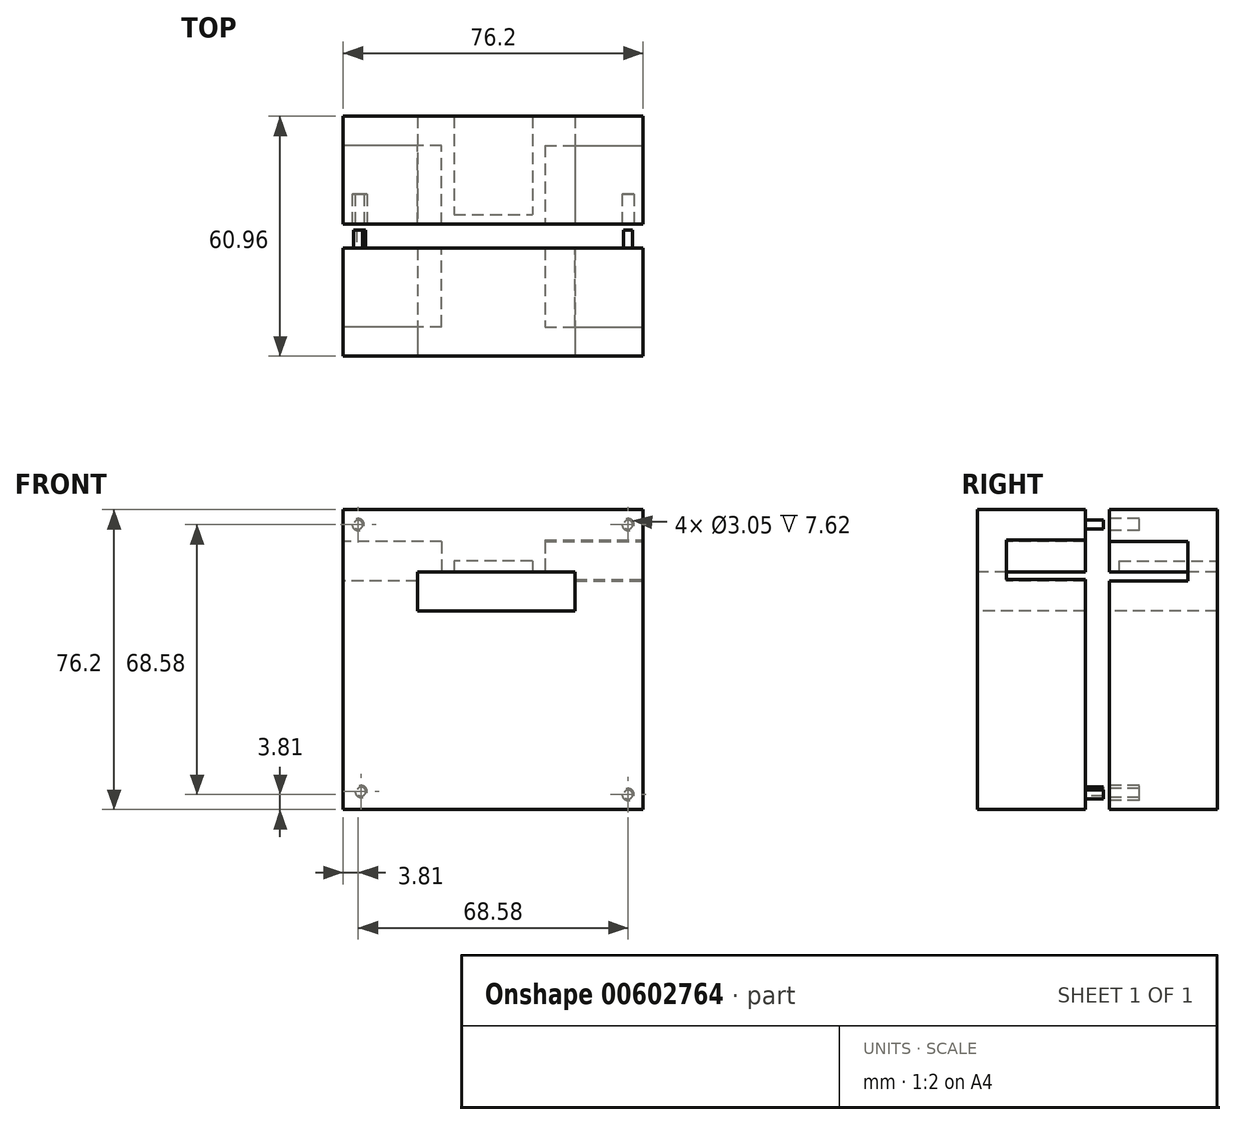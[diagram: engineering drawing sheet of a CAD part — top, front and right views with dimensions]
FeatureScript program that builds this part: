
annotation { "Feature Type Name" : "Feature", "Feature Type Description" : "" }
export const myFeature = defineFeature(function(context is Context, id is Id, definition is map)
    precondition{}
    {
        {
            var Q0;
            Q0=qCreatedBy(makeId("Front.planeOp"),FACE);
            var sketch = newSketch(context, id + "F0", { "sketchPlane" : qUnion([Q0])});
            skLineSegment(sketch, "E0.bottom", {"start": v(-63.5, 63.5) * mm, "end": v(63.5, 63.5) * mm});
            skLineSegment(sketch, "E0.top", {"start": v(-63.5, -63.5) * mm, "end": v(63.5, -63.5) * mm});
            skLineSegment(sketch, "E0.left", {"start": v(-63.5, 63.5) * mm, "end": v(-63.5, -63.5) * mm});
            skLineSegment(sketch, "E0.right", {"start": v(63.5, 63.5) * mm, "end": v(63.5, -63.5) * mm});
            skPoint(sketch, "E0.middle", {"position": v(0, 0) * mm});
            skSolve(sketch);
        }
        {
            var Q0;
            Q0=makeQuery(id+"F0.imprint","IMPRINT",FACE,{"disambiguationData":[TD([[makeQuery(id+"F0.imprint","IMPRINT",EDGE,{"derivedFrom":sQuery(id+"F0.wireOp",EDGE,"E0.bottom")}),-1.0]])]});
            extrude(context, id + "F1", {"entities" : qUnion([Q0]), "endBound" : BoundingType.SYMMETRIC, "depth" : 101.6 * mm, "offsetDistance" : 25.4 * mm});
        }
        {
            var Q0;
            Q0=makeQuery(id+"F1.opExtrude","SWEPT_FACE",FACE,{"disambiguationData":[OSD([sQuery(id+"F0.wireOp",EDGE,"E0.left")])]});
            var sketch = newSketch(context, id + "F2", { "sketchPlane" : qUnion([Q0])});
            skLineSegment(sketch, "E1.bottom", {"start": v(-5.1, 63.5) * mm, "end": v(5.1, 63.5) * mm});
            skLineSegment(sketch, "E1.top", {"start": v(-5.1, -63.5) * mm, "end": v(5.1, -63.5) * mm});
            skLineSegment(sketch, "E1.left", {"start": v(-5.1, 63.5) * mm, "end": v(-5.1, -63.5) * mm});
            skLineSegment(sketch, "E1.right", {"start": v(5.1, 63.5) * mm, "end": v(5.1, -63.5) * mm});
            skPoint(sketch, "E1.middle", {"position": v(0, 0) * mm});
            skPoint(sketch, "E1.middle.positionSnap0", {"position": v(0, 63.5) * mm});
            skPoint(sketch, "E1.middle.positionSnap1", {"position": v(-50.8, 0) * mm});
            skPoint(sketch, "E1.centerSnap0", {"position": v(0, 63.5) * mm});
            skPoint(sketch, "E1.centerSnap1", {"position": v(-50.8, 0) * mm});
            skSolve(sketch);
        }
        {
            var Q0;
            Q0=makeQuery(id+"F2.imprint","IMPRINT",FACE,{"disambiguationData":[TD([[makeQuery(id+"F2.imprint","IMPRINT",EDGE,{"derivedFrom":sQuery(id+"F2.wireOp",EDGE,"E1.bottom")}),1.0]])]});
            extrude(context, id + "F3", {"entities" : qUnion([Q0]), "operationType" : NewBodyOperationType.REMOVE, "oppositeDirection" : true, "depth" : 127 * mm, "offsetDistance" : 25.4 * mm});
        }
        {
            var Q0;
            Q0=makeQuery(id+"F3.boolean.opBoolean","COPY",FACE,{"derivedFrom":makeQuery(id+"F3.opExtrude","SWEPT_FACE",FACE,{"disambiguationData":[OSD([sQuery(id+"F2.wireOp",EDGE,"E1.left")])]})});
            var sketch = newSketch(context, id + "F4", { "sketchPlane" : qUnion([Q0])});
            skCircle(sketch, "E2", {"center": v(-57.15, 57.15) * mm, "radius": 2.54 * mm});
            skCircle(sketch, "E3", {"center": v(57.15, 57.15) * mm, "radius": 2.54 * mm});
            skCircle(sketch, "E4", {"center": v(57.15, -57.15) * mm, "radius": 2.54 * mm});
            skCircle(sketch, "E5", {"center": v(-55.88, -55.88) * mm, "radius": 2.54 * mm});
            skSolve(sketch);
        }
        {
            var Q0;
            Q0=makeQuery(id+"F3.boolean.opBoolean","COPY",FACE,{"derivedFrom":makeQuery(id+"F3.opExtrude","SWEPT_FACE",FACE,{"disambiguationData":[OSD([sQuery(id+"F2.wireOp",EDGE,"E1.right")])]})});
            var sketch = newSketch(context, id + "F5", { "sketchPlane" : qUnion([Q0])});
            skCircle(sketch, "E6", {"center": v(57.15, 57.15) * mm, "radius": 1.9 * mm});
            skCircle(sketch, "E7", {"center": v(-57.15, -57.15) * mm, "radius": 1.9 * mm});
            skCircle(sketch, "E8", {"center": v(-57.15, 57.15) * mm, "radius": 1.9 * mm});
            skCircle(sketch, "E9", {"center": v(55.88, -55.88) * mm, "radius": 1.9 * mm});
            skSolve(sketch);
        }
        {
            var Q0;
            Q0 = qSketchRegion(id + "F4", true);
            extrude(context, id + "F6", {"entities" : qUnion([Q0]), "operationType" : NewBodyOperationType.REMOVE, "oppositeDirection" : true, "depth" : 12.7 * mm, "offsetDistance" : 25.4 * mm});
        }
        {
            var Q0;
            Q0 = qSketchRegion(id + "F5", true);
            extrude(context, id + "F7", {"entities" : qUnion([Q0]), "operationType" : NewBodyOperationType.ADD, "depth" : 7.62 * mm, "offsetDistance" : 25.4 * mm});
        }
        {
            var Q0;
            Q0=makeQuery(id+"F3.boolean.opBoolean","SPLIT",BODY,{"disambiguationData":[OD(1.0)],"derivedFrom":makeQuery(id+"F1.opExtrude","SWEPT_BODY",BODY,{"disambiguationData":[OSD([sQuery(id+"F0.wireOp",EDGE,"E0.bottom"),sQuery(id+"F0.wireOp",EDGE,"E0.top"),sQuery(id+"F0.wireOp",EDGE,"E0.left"),sQuery(id+"F0.wireOp",EDGE,"E0.right")])]})});
            var Q1;
            Q1=makeQuery(id+"F3.boolean.opBoolean","SPLIT",BODY,{"disambiguationData":[OD(0.0)],"derivedFrom":makeQuery(id+"F1.opExtrude","SWEPT_BODY",BODY,{"disambiguationData":[OSD([sQuery(id+"F0.wireOp",EDGE,"E0.bottom"),sQuery(id+"F0.wireOp",EDGE,"E0.top"),sQuery(id+"F0.wireOp",EDGE,"E0.left"),sQuery(id+"F0.wireOp",EDGE,"E0.right")])]})});
            var Q2;
            Q2=qCreatedBy(makeId("Origin.pointOp"),VERTEX);
            transform(context, id + "F8", {"entities" : qUnion([Q0, Q1]), "transformType" : TransformType.SCALE_UNIFORMLY, "scale" : 0.6, "scalePoint" : qUnion([Q2]), "makeCopy" : false});
        }
        {
            var Q0;
            Q0=makeQuery(id+"F1.opExtrude","CAP_FACE",FACE,{"disambiguationData":[OSD([sQuery(id+"F0.wireOp",EDGE,"E0.bottom"),sQuery(id+"F0.wireOp",EDGE,"E0.top"),sQuery(id+"F0.wireOp",EDGE,"E0.left"),sQuery(id+"F0.wireOp",EDGE,"E0.right")])],"isStart":false});
            var sketch = newSketch(context, id + "F9", { "sketchPlane" : qUnion([Q0])});
            skLineSegment(sketch, "E10.bottom", {"start": v(-19.17, 22.33) * mm, "end": v(20.83, 22.33) * mm});
            skLineSegment(sketch, "E10.top", {"start": v(-19.17, 12.33) * mm, "end": v(20.83, 12.33) * mm});
            skLineSegment(sketch, "E10.left", {"start": v(-19.17, 22.33) * mm, "end": v(-19.17, 12.33) * mm});
            skLineSegment(sketch, "E10.right", {"start": v(20.83, 22.33) * mm, "end": v(20.83, 12.33) * mm});
            skPoint(sketch, "E10.middle", {"position": v(0.83, 17.33) * mm});
            skSolve(sketch);
        }
        {
            var Q0;
            Q0 = qSketchRegion(id + "F9", true);
            extrude(context, id + "F10", {"entities" : qUnion([Q0]), "operationType" : NewBodyOperationType.REMOVE, "oppositeDirection" : true, "depth" : 80 * mm, "offsetDistance" : 25 * mm});
        }
        {
            var Q0;
            Q0=makeQuery(id+"F1.opExtrude","CAP_FACE",FACE,{"disambiguationData":[OSD([sQuery(id+"F0.wireOp",EDGE,"E0.bottom"),sQuery(id+"F0.wireOp",EDGE,"E0.top"),sQuery(id+"F0.wireOp",EDGE,"E0.left"),sQuery(id+"F0.wireOp",EDGE,"E0.right")])],"isStart":true});
            var sketch = newSketch(context, id + "F11", { "sketchPlane" : qUnion([Q0])});
            skLineSegment(sketch, "E11.bottom", {"start": v(-10, 25) * mm, "end": v(10, 25) * mm});
            skLineSegment(sketch, "E11.top", {"start": v(-10, 15) * mm, "end": v(10, 15) * mm});
            skLineSegment(sketch, "E11.left", {"start": v(-10, 25) * mm, "end": v(-10, 15) * mm});
            skLineSegment(sketch, "E11.right", {"start": v(10, 25) * mm, "end": v(10, 15) * mm});
            skPoint(sketch, "E11.middle", {"position": v(0, 20) * mm});
            skSolve(sketch);
        }
        {
            var Q0;
            Q0 = qSketchRegion(id + "F11", true);
            extrude(context, id + "F12", {"entities" : qUnion([Q0]), "operationType" : NewBodyOperationType.REMOVE, "oppositeDirection" : true, "depth" : 25 * mm, "offsetDistance" : 25 * mm});
        }
        {
            var Q0;
            {var subQ1=sQuery(id+"F0.wireOp",EDGE,"E0.left");Q0=makeQuery(id+"F3.boolean.opBoolean","SPLIT",FACE,{"disambiguationData":[TD([makeQuery(id+"F3.opExtrude","SWEPT_FACE",FACE,{"disambiguationData":[OSD([sQuery(id+"F2.wireOp",EDGE,"E1.left")])]})])],"derivedFrom":makeQuery(id+"F1.opExtrude","SWEPT_FACE",FACE,{"disambiguationData":[OSD([subQ1])]})});}
            var sketch = newSketch(context, id + "F13", { "sketchPlane" : qUnion([Q0])});
            skLineSegment(sketch, "E12", {"start": v(-3.05, 0) * mm, "end": v(-3.05, 20) * mm});
            skLineSegment(sketch, "E13.bottom", {"start": v(-3.05, 20) * mm, "end": v(-23.05, 20) * mm});
            skLineSegment(sketch, "E13.top", {"start": v(-3.05, 30) * mm, "end": v(-23.05, 30) * mm});
            skLineSegment(sketch, "E13.left", {"start": v(-3.05, 20) * mm, "end": v(-3.05, 30) * mm});
            skLineSegment(sketch, "E13.right", {"start": v(-23.05, 20) * mm, "end": v(-23.05, 30) * mm});
            skSolve(sketch);
        }
        {
            var Q0;
            Q0 = qSketchRegion(id + "F13", true);
            extrude(context, id + "F14", {"entities" : qUnion([Q0]), "operationType" : NewBodyOperationType.REMOVE, "oppositeDirection" : true, "depth" : 25 * mm, "offsetDistance" : 25 * mm});
        }
        {
            var Q0;
            {var subQ1=sQuery(id+"F0.wireOp",EDGE,"E0.left");Q0=makeQuery(id+"F3.boolean.opBoolean","SPLIT",FACE,{"disambiguationData":[TD([makeQuery(id+"F3.opExtrude","SWEPT_FACE",FACE,{"disambiguationData":[OSD([sQuery(id+"F2.wireOp",EDGE,"E1.right")])]})])],"derivedFrom":makeQuery(id+"F1.opExtrude","SWEPT_FACE",FACE,{"disambiguationData":[OSD([subQ1])]})});}
            var sketch = newSketch(context, id + "F15", { "sketchPlane" : qUnion([Q0])});
            skLineSegment(sketch, "E14.bottom", {"start": v(3.05, 20) * mm, "end": v(23.05, 20) * mm});
            skLineSegment(sketch, "E14.top", {"start": v(3.05, 30) * mm, "end": v(23.05, 30) * mm});
            skLineSegment(sketch, "E14.left", {"start": v(3.05, 20) * mm, "end": v(3.05, 30) * mm});
            skLineSegment(sketch, "E14.right", {"start": v(23.05, 20) * mm, "end": v(23.05, 30) * mm});
            skSolve(sketch);
        }
        {
            var Q0;
            Q0 = qSketchRegion(id + "F15", true);
            extrude(context, id + "F16", {"entities" : qUnion([Q0]), "operationType" : NewBodyOperationType.REMOVE, "oppositeDirection" : true, "depth" : 25 * mm, "offsetDistance" : 25 * mm});
        }
        {
            var Q0;
            {var subQ1=sQuery(id+"F0.wireOp",EDGE,"E0.right");Q0=makeQuery(id+"F3.boolean.opBoolean","SPLIT",FACE,{"disambiguationData":[TD([makeQuery(id+"F3.opExtrude","SWEPT_FACE",FACE,{"disambiguationData":[OSD([sQuery(id+"F2.wireOp",EDGE,"E1.right")])]})])],"derivedFrom":makeQuery(id+"F1.opExtrude","SWEPT_FACE",FACE,{"disambiguationData":[OSD([subQ1])]})});}
            var sketch = newSketch(context, id + "F17", { "sketchPlane" : qUnion([Q0])});
            skLineSegment(sketch, "E15.bottom", {"start": v(-3.05, 20.34) * mm, "end": v(-23.05, 20.34) * mm});
            skLineSegment(sketch, "E15.top", {"start": v(-3.05, 30.34) * mm, "end": v(-23.05, 30.34) * mm});
            skLineSegment(sketch, "E15.left", {"start": v(-3.05, 20.34) * mm, "end": v(-3.05, 30.34) * mm});
            skLineSegment(sketch, "E15.right", {"start": v(-23.05, 20.34) * mm, "end": v(-23.05, 30.34) * mm});
            skSolve(sketch);
        }
        {
            var Q0;
            Q0 = qSketchRegion(id + "F17", true);
            extrude(context, id + "F18", {"entities" : qUnion([Q0]), "operationType" : NewBodyOperationType.REMOVE, "oppositeDirection" : true, "depth" : 25 * mm, "offsetDistance" : 25 * mm});
        }
        {
            var Q0;
            {var subQ1=sQuery(id+"F0.wireOp",EDGE,"E0.right");Q0=makeQuery(id+"F3.boolean.opBoolean","SPLIT",FACE,{"disambiguationData":[TD([makeQuery(id+"F3.opExtrude","SWEPT_FACE",FACE,{"disambiguationData":[OSD([sQuery(id+"F2.wireOp",EDGE,"E1.left")])]})])],"derivedFrom":makeQuery(id+"F1.opExtrude","SWEPT_FACE",FACE,{"disambiguationData":[OSD([subQ1])]})});}
            var sketch = newSketch(context, id + "F19", { "sketchPlane" : qUnion([Q0])});
            skLineSegment(sketch, "E16", {"start": v(3.05, 0) * mm, "end": v(3.05, 20) * mm});
            skLineSegment(sketch, "E17.bottom", {"start": v(3.05, 20) * mm, "end": v(23.05, 20) * mm});
            skLineSegment(sketch, "E17.top", {"start": v(3.05, 30) * mm, "end": v(23.05, 30) * mm});
            skLineSegment(sketch, "E17.left", {"start": v(3.05, 20) * mm, "end": v(3.05, 30) * mm});
            skLineSegment(sketch, "E17.right", {"start": v(23.05, 20) * mm, "end": v(23.05, 30) * mm});
            skSolve(sketch);
        }
        {
            var Q0;
            Q0 = qSketchRegion(id + "F19", true);
            extrude(context, id + "F20", {"entities" : qUnion([Q0]), "operationType" : NewBodyOperationType.REMOVE, "oppositeDirection" : true, "depth" : 25 * mm, "offsetDistance" : 25 * mm});
        }
        {
            var Q0;
            Q0=qCreatedBy(makeId("Right.planeOp"),FACE);
            var sketch = newSketch(context, id + "F21", { "sketchPlane" : qUnion([Q0])});
            skLineSegment(sketch, "E18", {"start": v(0, 0) * mm, "end": v(68.46, 0) * mm});
            skSolve(sketch);
        }
        {
            var Q0;
            Q0=makeQuery(id+"F3.boolean.opBoolean","SPLIT",BODY,{"disambiguationData":[OD(0.0)],"derivedFrom":makeQuery(id+"F1.opExtrude","SWEPT_BODY",BODY,{"disambiguationData":[OSD([sQuery(id+"F0.wireOp",EDGE,"E0.bottom"),sQuery(id+"F0.wireOp",EDGE,"E0.top"),sQuery(id+"F0.wireOp",EDGE,"E0.left"),sQuery(id+"F0.wireOp",EDGE,"E0.right")])]})});
            var Q1;
            Q1=sQuery(id+"F21.wireOp",EDGE,"E18");
            transform(context, id + "F22", {"entities" : qUnion([Q0]), "transformType" : TransformType.TRANSLATION_ENTITY, "oppositeDirectionEntity" : false, "transformLine" : qUnion([Q1]), "makeCopy" : false});
        }
    });
